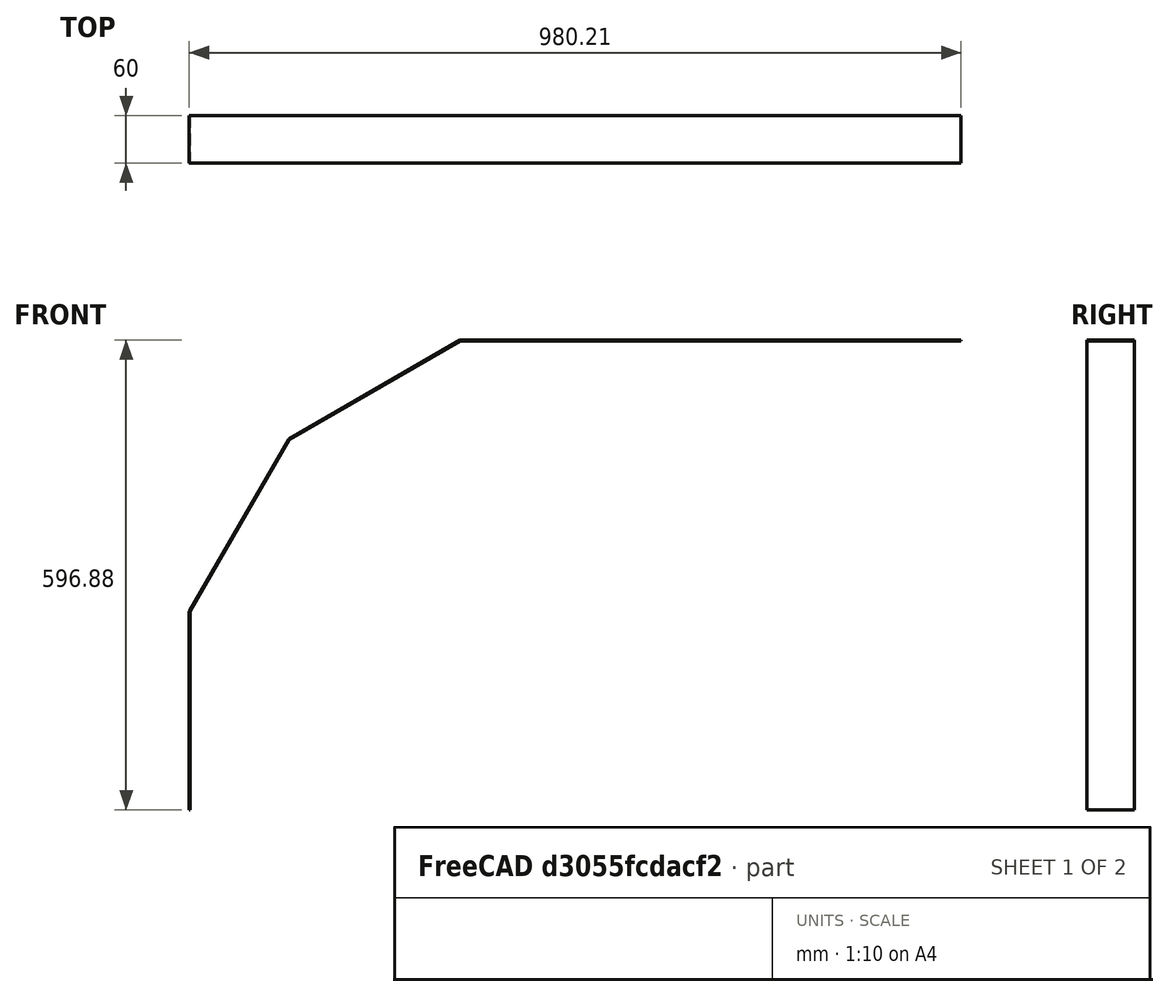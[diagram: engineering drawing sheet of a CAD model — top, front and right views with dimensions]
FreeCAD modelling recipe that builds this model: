
FCSTD DOCUMENT  (FreeCAD 0.18.4R)
Label: LowPolyPannierMudguard
License: All rights reserved
LicenseURL: http://en.wikipedia.org/wiki/All_rights_reserved
objects: Spreadsheet::Sheet×1, Sketcher::SketchObject×1, PartDesign::FeaturePython×1, PartDesign::Body×1
note: 3 computed .brp shape members not serialized (recipe doc carries the construction recipe); baked Part::Feature solids carry a one-line shape summary decoded from their .brp

FEATURE [Spreadsheet::Sheet] Spreadsheet
  cells = A2=Wheel Diameter; B2(WheelDiameter)==26.5"; A3=Tyre Thickness; B3(TyreThickness)==2"; A4=Mudguard Clearance; B4(MudguardClearance)==100mm; A6=Mudguard Width; B6(MudguardWidth)==60mm
FEATURE [Sketcher::SketchObject] Sketch
  MapMode = 5
  Placement = pos=(0,0,0) rot=(1,0,0;1.5708rad)
  Support = -> [XZ_Plane]
  expr: Constraints[5] = Spreadsheet.WheelDiameter + 2 * (Spreadsheet.TyreThickness + Spreadsheet.MudguardClearance)
  expr: Constraints[4] = Spreadsheet.WheelDiameter + 2 * Spreadsheet.TyreThickness
  expr: Constraints[3] = Spreadsheet.WheelDiameter
  sketch-geometry (7):
    g0: Circle [constr] CenterX=0 CenterY=0 CenterZ=0 NormalX=0 NormalY=0 NormalZ=1 AngleXU=0 Radius=336.55
    g1: Circle [constr] CenterX=0 CenterY=0 CenterZ=0 NormalX=0 NormalY=0 NormalZ=1 AngleXU=0 Radius=387.35
    g2: Circle [constr] CenterX=0 CenterY=0 CenterZ=0 NormalX=0 NormalY=0 NormalZ=1 AngleXU=0 Radius=487.35
    g3: LineSegment StartX=509.474 StartY=470.744 StartZ=0 EndX=-126.135 EndY=470.744 EndZ=0
    g4: LineSegment StartX=-126.135 StartY=470.744 StartZ=0 EndX=-344.608 EndY=344.608 EndZ=0
    g5: LineSegment StartX=-344.608 StartY=344.608 StartZ=0 EndX=-470.744 EndY=126.135 EndZ=0
    g6: LineSegment StartX=-470.744 StartY=126.135 StartZ=0 EndX=-470.744 EndY=-126.135 EndZ=0
  constraints (18):
    c: Coincident(g0,g-1)
    c: Coincident(g1,g0)
    c: Coincident(g2,g0)
    c: Diameter(g0) = 673.1
    c: Diameter(g1) = 774.7
    c: Diameter(g2) = 974.7
    c: PointOnObject(g3,g2)
    c: Horizontal(g3)
    c: Coincident(g3,g4)
    c: PointOnObject(g4,g2)
    c: Coincident(g4,g5)
    c: Coincident(g5,g6)
    c: PointOnObject(g6,g2)
    c: Vertical(g6)
    c: PointOnObject(g5,g2)
    c: Angle(g4,g3) = 2.61799
    c: Angle(g5,g4) = 2.61799
    c: Equal(g5,g4)
FEATURE [PartDesign::FeaturePython] BaseBend  # WARN: FeaturePython — macro-defined, semantics opaque (R4)
  BendSide = 0
  BendSketch = -> Sketch
  MidPlane = false
  Reverse = false
  length = 60
  radius = 1
  thickness = 1
  expr: length = Spreadsheet.MudguardWidth
FEATURE [PartDesign::Body] Body
  Group = -> [Sketch,BaseBend]
  Origin = -> Origin
  Tip = -> BaseBend
